# Revit family: KEUCO_51689010100
name_source: partatom
category: Sonderausstattung
revit_build: Autodesk Revit 2016 (Build: 20150220_1215(x64)
units: mm (PartAtom-declared; Revit-internal decimal feet)

## family parameters
Arbeitsebenenbasiert = Nein
Beim Laden mit Abzugskörper schneiden = Nein
Bemaßung runder Anschluss = Durchmesser verwenden
Gemeinsam genutzt = Nein
Immer vertikal = Ja
OmniClass-Nummer = 23.45.05.00
Raumberechnungspunkt = Nein
Teiletyp = Normal

## types (2) — shared parameters
Beschreibung = für Deckenanschluß G 1/2, mit runder Rosette
Hersteller = KEUCO
Kategorie = ARM
KreisBase = Ja
Preisgruppe = 1
Serie = Elegance
URL = https://www.keuco.com
Verwendung = DU / WA
ViereckBase = Nein

## per-type parameters (varying)
| type | Armelänge | Ausschreibungstext | Gewicht |
| 51689010300 | 300 mm | KEUCO Brausearm für Deckenanschluss 51689010300 
Hochglanzverchromter Brausearm für Deckenanschluss,
G 1/2, mit runder Rosette, 
Durchmesser der Rosette 80 mm,
Möglichkeit zur Ausrichtung zur Wand (90° ± 2°) und 
zum Wandanschluss (90° ± 5°),
Ausladung:300 mm

Hinweis:
Passende UP Funktionseinheit
59547000170 | 1.37 |
| 51689010100 | 100 mm  [stored 0.328084 ft] | KEUCO Brausearm für Deckenanschluss    51689010100 
hochglanzverchromter Brausearm für Deckenanschluss,
G 1/2, mit runder Rosette, Durchmesser 60 mm
Ausladung:100 mm | 9.4 |

note: column(s) folded — value = type name in every type: Artikelnummer

note: [stored X ft] marks values corroborated as IEEE doubles in the binary element streams (Revit-internal decimal feet)

## geometry (parser evidence)
native form markers: Blend x2, Sweep x3
no freeform markers — native parametric forms only
